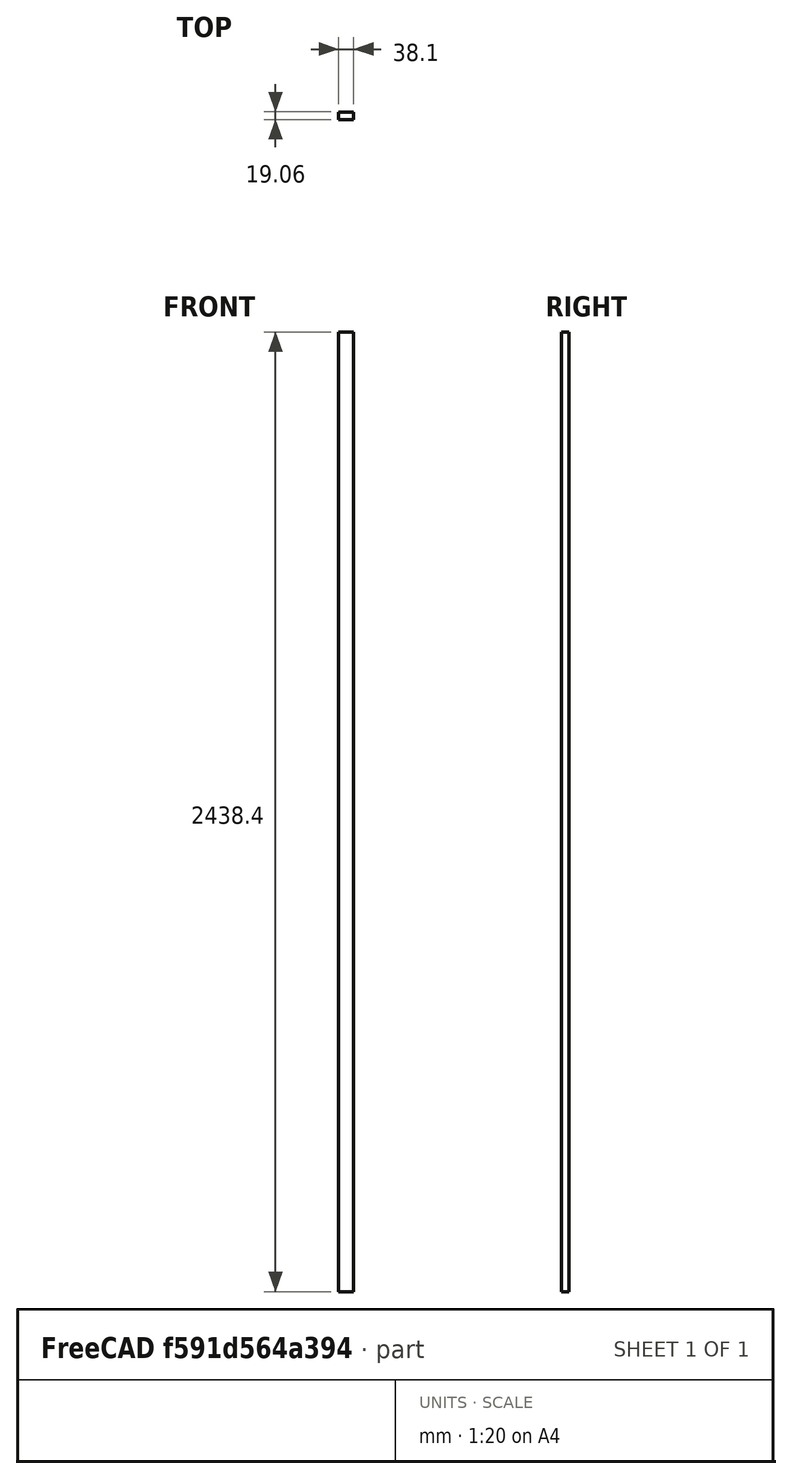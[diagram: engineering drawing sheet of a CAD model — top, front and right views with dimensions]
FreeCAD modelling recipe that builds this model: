
FCSTD DOCUMENT  (FreeCAD 0.21R33771 (Git))
Label: 1x2x8
License: All rights reserved
LicenseURL: http://en.wikipedia.org/wiki/All_rights_reserved
objects: Spreadsheet::Sheet×1, Sketcher::SketchObject×1, PartDesign::Pad×1, PartDesign::Body×1
note: 4 computed .brp shape members not serialized (recipe doc carries the construction recipe); baked Part::Feature solids carry a one-line shape summary decoded from their .brp

FEATURE [Spreadsheet::Sheet] Spreadsheet  label="var"
  cells = A2='varname; A3='len; B3(len)==25.4 * 96; A4='wid; B4(wid)==25.4 * 1.5; A5='thk; B5(thk)==25.4 * 0.75
FEATURE [Sketcher::SketchObject] Sketch
  FullyConstrained = true
  MapMode = 5
  Support = -> [XY_Plane]
  expr: Constraints[10] = <<var>>.thk
  expr: Constraints[9] = <<var>>.wid
  sketch-geometry (4):
    g0: LineSegment StartX=-19.05 StartY=9.525 StartZ=0 EndX=19.05 EndY=9.525 EndZ=0
    g1: LineSegment StartX=19.05 StartY=9.525 StartZ=0 EndX=19.05 EndY=-9.525 EndZ=0
    g2: LineSegment StartX=19.05 StartY=-9.525 StartZ=0 EndX=-19.05 EndY=-9.525 EndZ=0
    g3: LineSegment StartX=-19.05 StartY=-9.525 StartZ=0 EndX=-19.05 EndY=9.525 EndZ=0
  constraints (11):
    c: Coincident(g0,g1)
    c: Coincident(g1,g2)
    c: Coincident(g2,g3)
    c: Coincident(g3,g0)
    c: Horizontal(g0)
    c: Horizontal(g2)
    c: Vertical(g1)
    c: Vertical(g3)
    c: Symmetric(g0,g2,g-1)
    c: Distance(g0,g0) = 38.1
    c: Distance(g0,g2) = 19.05
FEATURE [PartDesign::Pad] Pad
  Direction = (0,0,1)
  Length = 2438.4
  Length2 = 10
  Profile = -> Sketch
  ReferenceAxis = -> Sketch [N_Axis]
  Type = 0
  expr: Length = <<var>>.len
FEATURE [PartDesign::Body] Body
  Group = -> [Sketch,Pad]
  Origin = -> Origin
  Tip = -> Pad
